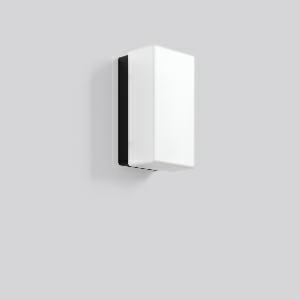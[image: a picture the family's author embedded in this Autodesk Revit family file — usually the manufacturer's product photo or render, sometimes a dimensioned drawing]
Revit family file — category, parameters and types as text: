
# Revit family: rechteck_21146_003_5e70
name_source: partatom
category: Lighting Fixtures
units: mm (PartAtom-declared; Revit-internal decimal feet)

## family parameters
Cut with Voids When Loaded = No
Host = Face
Light Source = No
Part Type = Normal
Room Calculation Point = No
Round Connector Dimension = Use Diameter
Shared = No

## types (1)
- RECHTECK (1 x QA60/clear E27, 700 lm, 46 W, 3000)
    Apparent Load = 46 VA
    CIE Flux Codes = 35 64 86 74 50
    Color Rendering = 90
    Color Temperature = 3000
    Default Elevation = 1800 mm
    Description = Series: RECHTECK
Rectangular surface-mounted luminaire in classic design. Base: plastic. Opal glass: mouth-blown, satin finish. Diffuser fastening: spring system. Suitable for Ceiling mounting, Wall (surface). IP 43 ceiling mounting, IP 44 wall mounting. 
Colour: black
Length: 220 mm
Width: 120 mm
Height: 105 mm
Lamp: A60
Number of lamps: 1
Wattage: 60 W
Socket: E27
System power: 46 W
Rated luminous flux: 350 lm
Luminous efficiency: 8 lm/W
Control gear: Converter not necessary
Protection class: II
Type of protection: IP 43
    Height = 105 mm
    Lamp = 1 x QA60/clear E27
    Lamp Light Flux = 700 lm
    Lamp Power = 46 W
    Lamp count = 1
    Length = 220 mm
    Lifetime = 3000 h
    Luminous efficacy = 8 lm/W
    Manufacturer = RZB
    ModVariant = No
    Model = 21146.003
    Mounting Place = Ceiling, Wall
    Mounting Type = Surface mounted
    Number of Poles = 1
    OnlyDefault = Yes
    Power Factor = 1
    Product Name = RECHTECK
    Product group = Surface mounted ceiling and wall luminaires
    ProductGroupID = 305
    Protection Class = Protection class II
    Protection Degree = IP 43
    RLX_Detail_Level = 1
    RLX_Emergency_Light_Flux = 0 lm
    RLX_Emergency_Type = 0
    RLX_Emergency_Type_DB = No
    RlxData = <blob elided: 20105 chars, md5=cd972430>
    Socket = E27
    Standby Power = 0 W
    System Light Flux = 352 lm
    System Power = 46 W
    Type Comments = Product without accessories
    Type Image = 21146.003.jpg
    URL = http://relux.com
    VarID = ---
    Voltage = 230 V
    Voltage Range = 220-240 V
    Weight = 0.00 kg
    Width = 120 mm

## geometry (parser evidence)
native form markers: Blend x4, Sweep x14
no freeform markers — native parametric forms only
